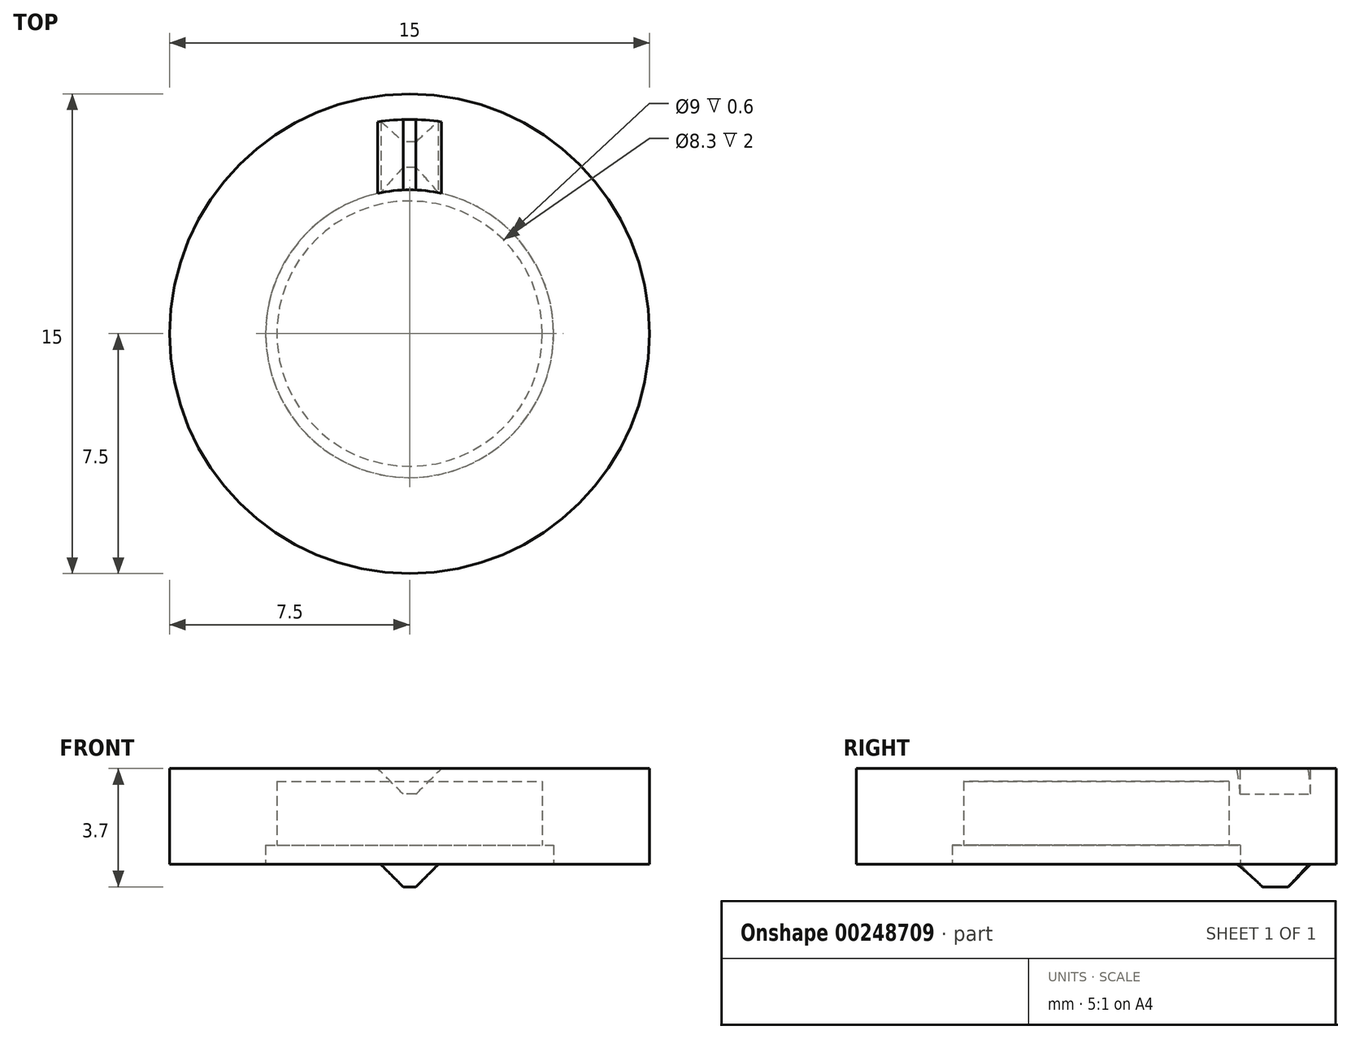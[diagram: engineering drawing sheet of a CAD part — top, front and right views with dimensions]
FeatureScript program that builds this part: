
annotation { "Feature Type Name" : "Feature", "Feature Type Description" : "" }
export const myFeature = defineFeature(function(context is Context, id is Id, definition is map)
    precondition{}
    {
        {
            var Q0;
            Q0=qCreatedBy(makeId("Top.planeOp"),FACE);
            var sketch = newSketch(context, id + "F0", { "sketchPlane" : qUnion([Q0])});
            skCircle(sketch, "E0", {"center": v(0, 0) * mm, "radius": 7.5 * mm});
            skSolve(sketch);
        }
        {
            var Q0;
            Q0 = qSketchRegion(id + "F0", true);
            extrude(context, id + "F1", {"entities" : qUnion([Q0]), "depth" : 3 * mm});
        }
        {
            var Q0;
            Q0=makeQuery(id+"F1.opExtrude","CAP_FACE",FACE,{"disambiguationData":[OSD([sQuery(id+"F0.wireOp",EDGE,"E0")])],"isStart":false});
            var sketch = newSketch(context, id + "F2", { "sketchPlane" : qUnion([Q0])});
            skLineSegment(sketch, "E1.bottom", {"start": v(1, 1.03) * mm, "end": v(-1, 1.03) * mm});
            skLineSegment(sketch, "E1.top", {"start": v(1, 13.97) * mm, "end": v(-1, 13.97) * mm});
            skLineSegment(sketch, "E1.left", {"start": v(1, 1.03) * mm, "end": v(1, 13.97) * mm});
            skLineSegment(sketch, "E1.right", {"start": v(-1, 1.03) * mm, "end": v(-1, 13.97) * mm});
            skPoint(sketch, "E1.middle", {"position": v(0, 7.5) * mm});
            skCircle(sketch, "E2.0", {"center": v(0, 0) * mm, "radius": 7.5 * mm});
            skCircle(sketch, "E3", {"center": v(0, 0) * mm, "radius": 4.5 * mm});
            skCircle(sketch, "E4", {"center": v(0, 0) * mm, "radius": 6.7 * mm});
            skSolve(sketch);
        }
        {
            var Q0;
            {var subQ0=sQuery(id+"F2.wireOp",EDGE,"E3");var subQ1=sQuery(id+"F2.wireOp",EDGE,"E1.left");var subQ2=makeQuery(id+"F2.imprint","INTERSECT",VERTEX,{"derivedFrom":[subQ1,subQ0]});Q0=makeQuery(id+"F2.imprint","IMPRINT",FACE,{"disambiguationData":[TD([[makeQuery(id+"F2.imprint","IMPRINT",EDGE,{"disambiguationData":[TD([[subQ2,-1.0]])],"derivedFrom":subQ1}),1.0]])]});}
            extrude(context, id + "F3", {"entities" : qUnion([Q0]), "operationType" : NewBodyOperationType.REMOVE, "oppositeDirection" : true, "depth" : 0.8 * mm});
        }
        {
            var Q0;
            Q0=makeQuery(id+"F3.boolean.opBoolean","COPY",EDGE,{"derivedFrom":makeQuery(id+"F3.opExtrude","CAP_EDGE",EDGE,{"disambiguationData":[OSD([sQuery(id+"F2.wireOp",EDGE,"E1.right")])],"isStart":false})});
            var Q1;
            Q1=makeQuery(id+"F3.boolean.opBoolean","COPY",EDGE,{"derivedFrom":makeQuery(id+"F3.opExtrude","CAP_EDGE",EDGE,{"disambiguationData":[OSD([sQuery(id+"F2.wireOp",EDGE,"E1.left")])],"isStart":false})});
            chamfer(context, id + "F4", {"entities" : qUnion([Q0, Q1]), "width" : 0.8 * mm, "tangentPropagation" : true});
        }
        {
            var Q0;
            Q0=makeQuery(id+"F1.opExtrude","CAP_FACE",FACE,{"disambiguationData":[OSD([sQuery(id+"F0.wireOp",EDGE,"E0")])],"isStart":true});
            var sketch = newSketch(context, id + "F5", { "sketchPlane" : qUnion([Q0])});
            skArc(sketch, "E5.0", {"start": v(1, -6.62) * mm, "mid": v(0, -6.7) * mm, "end": v(-1, -6.62) * mm});
            skArc(sketch, "E6.0", {"start": v(1, -4.39) * mm, "mid": v(0, -4.5) * mm, "end": v(-1, -4.39) * mm});
            skLineSegment(sketch, "E7.0", {"start": v(1, -4.39) * mm, "end": v(1, -6.62) * mm});
            skLineSegment(sketch, "E8.0", {"start": v(-1, -4.39) * mm, "end": v(-1, -6.62) * mm});
            skSolve(sketch);
        }
        {
            var Q0;
            Q0 = qSketchRegion(id + "F5", true);
            extrude(context, id + "F6", {"entities" : qUnion([Q0]), "operationType" : NewBodyOperationType.ADD, "depth" : 0.7 * mm});
        }
        {
            var Q0;
            Q0=makeQuery(id+"F6.opExtrude","CAP_EDGE",EDGE,{"disambiguationData":[OSD([sQuery(id+"F5.wireOp",EDGE,"E7.0")])],"isStart":false});
            var Q1;
            Q1=makeQuery(id+"F6.opExtrude","CAP_EDGE",EDGE,{"disambiguationData":[OSD([sQuery(id+"F5.wireOp",EDGE,"E8.0")])],"isStart":false});
            chamfer(context, id + "F7", {"entities" : qUnion([Q0, Q1]), "width" : 0.8 * mm, "tangentPropagation" : true});
        }
        {
            var Q0;
            Q0=makeQuery(id+"F6.opExtrude","CAP_EDGE",EDGE,{"disambiguationData":[OSD([sQuery(id+"F5.wireOp",EDGE,"E6.0")])],"isStart":false});
            var Q1;
            Q1=makeQuery(id+"F6.opExtrude","CAP_EDGE",EDGE,{"disambiguationData":[OSD([sQuery(id+"F5.wireOp",EDGE,"E5.0")])],"isStart":false});
            chamfer(context, id + "F8", {"entities" : qUnion([Q0, Q1]), "width" : 0.7 * mm, "tangentPropagation" : true});
        }
        {
            var Q0;
            Q0=makeQuery(id+"F1.opExtrude","CAP_FACE",FACE,{"disambiguationData":[OSD([sQuery(id+"F0.wireOp",EDGE,"E0")])],"isStart":true});
            var sketch = newSketch(context, id + "F9", { "sketchPlane" : qUnion([Q0])});
            skCircle(sketch, "E9", {"center": v(0, 0) * mm, "radius": 4.15 * mm});
            skSolve(sketch);
        }
        {
            var Q0;
            Q0 = qSketchRegion(id + "F9", true);
            extrude(context, id + "F10", {"entities" : qUnion([Q0]), "operationType" : NewBodyOperationType.REMOVE, "oppositeDirection" : true, "depth" : 2.6 * mm});
        }
        {
            var Q0;
            Q0=makeQuery(id+"F1.opExtrude","CAP_FACE",FACE,{"disambiguationData":[OSD([sQuery(id+"F0.wireOp",EDGE,"E0")])],"isStart":true});
            var sketch = newSketch(context, id + "F11", { "sketchPlane" : qUnion([Q0])});
            skCircle(sketch, "E10", {"center": v(0, 0) * mm, "radius": 4.5 * mm});
            skSolve(sketch);
        }
        {
            var Q0;
            Q0 = qSketchRegion(id + "F11", true);
            extrude(context, id + "F12", {"entities" : qUnion([Q0]), "operationType" : NewBodyOperationType.REMOVE, "oppositeDirection" : true, "depth" : 0.6 * mm});
        }
    });
